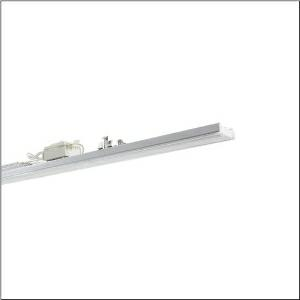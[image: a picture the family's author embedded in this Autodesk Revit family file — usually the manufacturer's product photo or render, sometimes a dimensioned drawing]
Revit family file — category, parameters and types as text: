
# Revit family: licross_r__11_recessed_ho_51te1edn4d5s_9b57
name_source: partatom
category: Lighting Fixtures
units: mm (PartAtom-declared; Revit-internal decimal feet)

## family parameters
Cut with Voids When Loaded = No
Host = Face
Light Source = No
Part Type = Normal
Room Calculation Point = No
Round Connector Dimension = Use Diameter
Shared = No

## types (1)
- --- (1 x LED, 13670 lm, 76.8 W, 4000K)
    Apparent Load = 77 VA
    CIE Flux Codes = 85 95 99 100 100
    Color Rendering = 80
    Color Temperature = 4000K
    Default Elevation = 1800 mm
    Description = Licross® 11 Recessed HO, luminaire insert, of sheet steel, galvanised, coil coated, white, length: 1.500mm, width: 66mm, height: 67mm, LED rated luminous flux: 13.670lm, light colour: 840, control gear: DALI 2, with plug, 5-pole, with phase selection, mains connection: 220..240V, AC, 50/60Hz, rated input power: 77W, halogen-free wiring, primary light control with lens, of plastic, primary optical cover: cover, of PMMA, light emission: direct distribution, primary light characteristic: symmetric, protection rating (complete): IP54, insulation class (complete): insulation class I (protective earthing), certification: CE, ENEC, VDE, UKCA, protection symbol: D if used in an environment with non-conductive dust loads with corresponding accessories, impact resistance: IK06, permissible ambient temperature for indoor applications: -25..+30°C, corresponds to IFS (International Featured Standards) requirements for safety and quality in the food industry, reducing of maximum allowable ambient temperature of 5°C with ceiling mounting, LABS conformity tested according to VDMA 24364:2018-05, packaging unit: 1 piece
    Height = 58 mm
    Lamp = 1 x LED
    Lamp Light Flux = 13670 lm
    Lamp Power = 76.8 W
    Lamp count = 1
    Length = 1500 mm
    Luminous efficacy = 178 lm/W
    Manufacturer = Siteco
    ModVariant = No
    Model = 51TE1EDN4D5S
    Mounting Place = Ceiling
    Mounting Type = Pendant
    Number of Poles = 1
    OnlyDefault = Yes
    Power Factor = 1
    Product Name = Licross® 11 Recessed HO
    Product group = luminaire insert
    ProductGroupID = 902
    Protection Class = Protection class I
    Protection Degree = IP 54
    RLX_Detail_Level = 1
    RLX_Emergency_Light_Flux = 0 lm
    RLX_Emergency_Type = 0
    RLX_Emergency_Type_DB = No
    RlxData = <blob elided: 24697 chars, md5=2654cec0>
    Socket = socket
    Standby Power = 0 W
    System Light Flux = 13670 lm
    System Power = 77 W
    Type Comments = factory setting: luminous flux: 100 % | dim-lin: 254 | 522 mA
    Type Image = l_1296930.jpg
    URL = http://relux.com
    VarID = @adj_095882
    Voltage = 0 V
    Weight = 0.00 kg
    Width = 66 mm

## geometry (parser evidence)
native form markers: Blend x4, Sweep x11
no freeform markers — native parametric forms only
